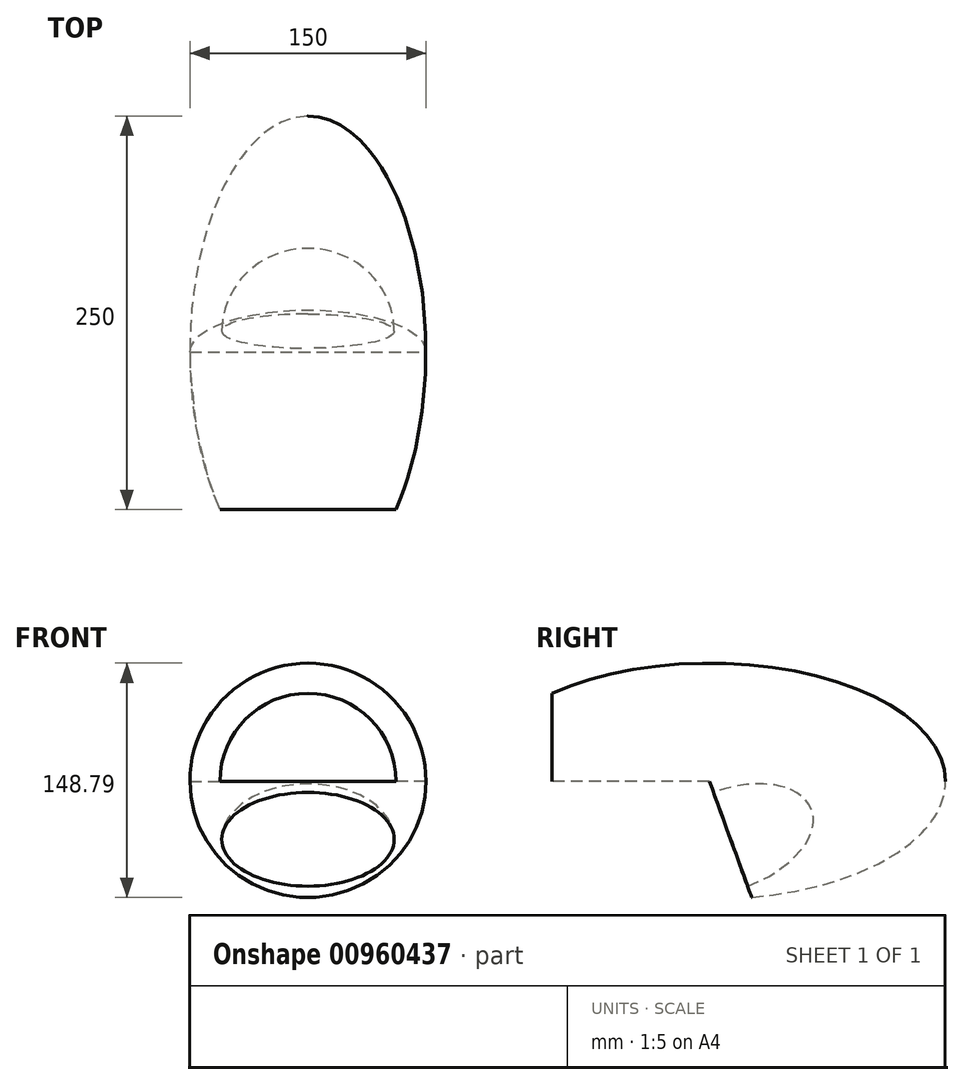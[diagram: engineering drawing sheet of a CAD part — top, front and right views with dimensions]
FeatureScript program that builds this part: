
annotation { "Feature Type Name" : "Feature", "Feature Type Description" : "" }
export const myFeature = defineFeature(function(context is Context, id is Id, definition is map)
    precondition{}
    {
        {
            var Q0;
            Q0=qCreatedBy(makeId("Right.planeOp"),FACE);
            var sketch = newSketch(context, id + "F0", { "sketchPlane" : qUnion([Q0])});
            skEllipticalArc(sketch, "E0", {});
            skLineSegment(sketch, "E1", {"start": v(-107.88, 0) * mm, "end": v(-66.03, 0) * mm, "construction": true});
            skLineSegment(sketch, "E2", {"start": v(-66.03, 0) * mm, "end": v(233.97, 0) * mm});
            skLineSegment(sketch, "E3", {"start": v(-16.03, 55.9) * mm, "end": v(-16.03, 0) * mm});
            skLineSegment(sketch, "E4.trimOffspring", {"start": v(-16.03, 0) * mm, "end": v(245.33, 0) * mm, "construction": true});
            const initialGuessF0  = {"E0": [0.0839694118076077, 0, -1, 0, 0.15, 0.075, 3.141592653589793, 5.442116636611656]};
            skSetInitialGuess(sketch, initialGuessF0);
            skSolve(sketch);
        }
        {
            var Q0;
            Q0 = qSketchRegion(id + "F0", true);
            var Q1;
            Q1=sQuery(id+"F0.wireOp",EDGE,"E1");
            revolve(context, id + "F1", {"surfaceOperationType" : NewSurfaceOperationType.NEW, "entities" : qUnion([Q0]), "axis" : qUnion([Q1]), "revolveType" : RevolveType.FULL});
        }
        {
            var Q0;
            Q0=qCreatedBy(makeId("Right.planeOp"),FACE);
            var sketch = newSketch(context, id + "F2", { "sketchPlane" : qUnion([Q0])});
            skLineSegment(sketch, "E5", {"start": v(-26.03, 0) * mm, "end": v(83.97, 0) * mm});
            skLineSegment(sketch, "E6", {"start": v(83.97, 0) * mm, "end": v(134.5, -138.85) * mm});
            skLineSegment(sketch, "E7", {"start": v(134.5, -138.85) * mm, "end": v(-26.03, -138.85) * mm});
            skLineSegment(sketch, "E8", {"start": v(-26.03, -138.85) * mm, "end": v(-26.03, 0) * mm});
            skSolve(sketch);
        }
        {
            var Q0;
            Q0=makeQuery(id+"F2.imprint","IMPRINT",FACE,{"disambiguationData":[TD([[makeQuery(id+"F2.imprint","IMPRINT",EDGE,{"derivedFrom":sQuery(id+"F2.wireOp",EDGE,"E5")}),-1.0]])]});
            extrude(context, id + "F3", {"entities" : qUnion([Q0]), "operationType" : NewBodyOperationType.REMOVE, "endBound" : BoundingType.SYMMETRIC, "oppositeDirection" : true, "depth" : 150 * mm, "offsetDistance" : 25 * mm});
        }
        {
            var Q0;
            Q0=makeQuery(id+"F3.boolean.opBoolean","COPY",FACE,{"derivedFrom":makeQuery(id+"F3.opExtrude","SWEPT_FACE",FACE,{"disambiguationData":[OSD([sQuery(id+"F2.wireOp",EDGE,"E6")])]})});
            var sketch = newSketch(context, id + "F4", { "sketchPlane" : qUnion([Q0])});
            skLineSegment(sketch, "E9", {"start": v(0, -28.72) * mm, "end": v(0, -107.24) * mm, "construction": true});
            skEllipticalArc(sketch, "E10", {});
            skLineSegment(sketch, "E11", {"start": v(0, -36.26) * mm, "end": v(0, -99.7) * mm});
            const initialGuessF4  = {"E10": [0, -0.06798104448950454, -1, 0, 0.05479004234075546, 0.0317176361713408, 1.5707963267948966, 4.71238898038469]};
            skSetInitialGuess(sketch, initialGuessF4);
            skSolve(sketch);
        }
        {
            var Q0;
            Q0 = qSketchRegion(id + "F4", true);
            var Q1;
            Q1=sQuery(id+"F4.wireOp",EDGE,"E9");
            revolve(context, id + "F5", {"operationType" : NewBodyOperationType.REMOVE, "surfaceOperationType" : NewSurfaceOperationType.NEW, "entities" : qUnion([Q0]), "axis" : qUnion([Q1]), "revolveType" : RevolveType.FULL, "oppositeDirection" : true});
        }
    });
